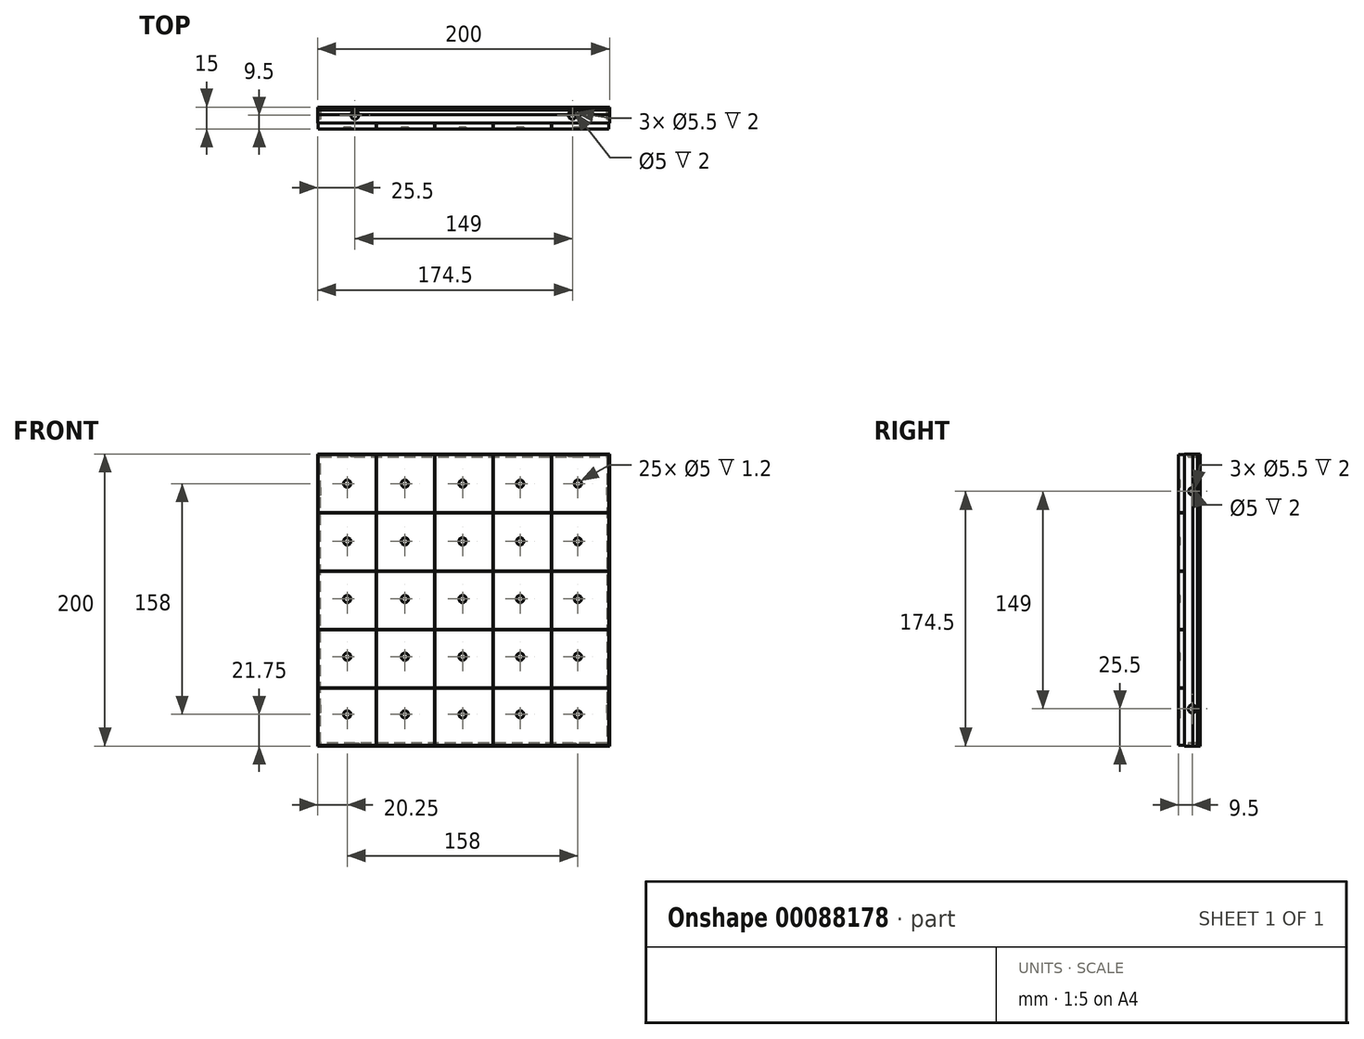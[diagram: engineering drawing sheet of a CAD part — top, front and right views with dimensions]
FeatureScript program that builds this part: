
annotation { "Feature Type Name" : "Feature", "Feature Type Description" : "" }
export const myFeature = defineFeature(function(context is Context, id is Id, definition is map)
    precondition{}
    {
        {
            var Q0;
            Q0=qCreatedBy(makeId("Front.planeOp"),FACE);
            var sketch = newSketch(context, id + "F0", { "sketchPlane" : qUnion([Q0])});
            skLineSegment(sketch, "E0.bottom", {"start": v(100, -100) * mm, "end": v(-100, -100) * mm});
            skLineSegment(sketch, "E0.top", {"start": v(100, 100) * mm, "end": v(-100, 100) * mm});
            skLineSegment(sketch, "E0.left", {"start": v(100, -100) * mm, "end": v(100, 100) * mm});
            skLineSegment(sketch, "E0.right", {"start": v(-100, -100) * mm, "end": v(-100, 100) * mm});
            skPoint(sketch, "E0.middle", {"position": v(0, 0) * mm});
            skSolve(sketch);
        }
        {
            var Q0;
            Q0=makeQuery(id+"F0.imprint","IMPRINT",FACE,{"disambiguationData":[TD([[makeQuery(id+"F0.imprint","IMPRINT",EDGE,{"derivedFrom":sQuery(id+"F0.wireOp",EDGE,"E0.bottom")}),-1.0]])]});
            var Q1;
            Q1 = qSketchRegion(id + "F0", true);
            extrude(context, id + "F1", {"entities" : qUnion([Q0, Q1]), "depth" : 15 * mm});
        }
        {
            var Q0;
            Q0=makeQuery(id+"F1.opExtrude","CAP_FACE",FACE,{"disambiguationData":[OSD([sQuery(id+"F0.wireOp",EDGE,"E0.bottom"),sQuery(id+"F0.wireOp",EDGE,"E0.top"),sQuery(id+"F0.wireOp",EDGE,"E0.left"),sQuery(id+"F0.wireOp",EDGE,"E0.right")])],"isStart":false});
            var sketch = newSketch(context, id + "F2", { "sketchPlane" : qUnion([Q0])});
            skLineSegment(sketch, "E1.bottom", {"start": v(-100, 100) * mm, "end": v(100, 100) * mm});
            skLineSegment(sketch, "E1.top", {"start": v(-100, 99.5) * mm, "end": v(100, 99.5) * mm});
            skLineSegment(sketch, "E1.left", {"start": v(-100, 100) * mm, "end": v(-100, 99.5) * mm});
            skLineSegment(sketch, "E1.right", {"start": v(100, 100) * mm, "end": v(100, 99.5) * mm});
            skLineSegment(sketch, "E2.0.1.0", {"start": v(-100, 59.5) * mm, "end": v(100, 59.5) * mm});
            skLineSegment(sketch, "E2.0.1.1", {"start": v(-100, 60) * mm, "end": v(100, 60) * mm});
            skLineSegment(sketch, "E2.0.1.2", {"start": v(100, 60) * mm, "end": v(100, 59.5) * mm});
            skLineSegment(sketch, "E2.0.1.3", {"start": v(-100, 60) * mm, "end": v(-100, 59.5) * mm});
            skLineSegment(sketch, "E2.0.2.0", {"start": v(-100, 19.5) * mm, "end": v(100, 19.5) * mm});
            skLineSegment(sketch, "E2.0.2.1", {"start": v(-100, 20) * mm, "end": v(100, 20) * mm});
            skLineSegment(sketch, "E2.0.2.2", {"start": v(100, 20) * mm, "end": v(100, 19.5) * mm});
            skLineSegment(sketch, "E2.0.2.3", {"start": v(-100, 20) * mm, "end": v(-100, 19.5) * mm});
            skLineSegment(sketch, "E2.0.3.0", {"start": v(-100, -20.5) * mm, "end": v(100, -20.5) * mm});
            skLineSegment(sketch, "E2.0.3.1", {"start": v(-100, -20) * mm, "end": v(100, -20) * mm});
            skLineSegment(sketch, "E2.0.3.2", {"start": v(100, -20) * mm, "end": v(100, -20.5) * mm});
            skLineSegment(sketch, "E2.0.3.3", {"start": v(-100, -20) * mm, "end": v(-100, -20.5) * mm});
            skLineSegment(sketch, "E2.0.4.0", {"start": v(-100, -60.5) * mm, "end": v(100, -60.5) * mm});
            skLineSegment(sketch, "E2.0.4.1", {"start": v(-100, -60) * mm, "end": v(100, -60) * mm});
            skLineSegment(sketch, "E2.0.4.2", {"start": v(100, -60) * mm, "end": v(100, -60.5) * mm});
            skLineSegment(sketch, "E2.0.4.3", {"start": v(-100, -60) * mm, "end": v(-100, -60.5) * mm});
            skLineSegment(sketch, "E2.direction1", {"start": v(-100, 99.5) * mm, "end": v(-99.9, 99.5) * mm, "construction": true});
            skLineSegment(sketch, "E2.direction2", {"start": v(-100, 99.5) * mm, "end": v(-100, 59.5) * mm, "construction": true});
            skLineSegment(sketch, "E3.0.0.5", {"start": v(-100, -100.5) * mm, "end": v(100, -100.5) * mm});
            skLineSegment(sketch, "E3.3.0.5", {"start": v(-100, -100) * mm, "end": v(100, -100) * mm});
            skLineSegment(sketch, "E3.6.0.5", {"start": v(100, -100) * mm, "end": v(100, -100.5) * mm});
            skLineSegment(sketch, "E3.9.0.5", {"start": v(-100, -100) * mm, "end": v(-100, -100.5) * mm});
            skSolve(sketch);
        }
        {
            var Q0;
            Q0 = qSketchRegion(id + "F0", true);
            extrude(context, id + "F3", {"entities" : qUnion([Q0]), "depth" : 5 * mm});
        }
        {
            var Q0;
            Q0 = qSketchRegion(id + "F2", true);
            extrude(context, id + "F4", {"entities" : qUnion([Q0]), "operationType" : NewBodyOperationType.REMOVE, "oppositeDirection" : true, "depth" : 4 * mm});
        }
        {
            var Q0;
            {var subQ0=sQuery(id+"F0.wireOp",EDGE,"E0.left");var subQ1=sQuery(id+"F0.wireOp",EDGE,"E0.right");Q0=makeQuery(id+"F4.boolean.opBoolean","SPLIT",FACE,{"disambiguationData":[TD([makeQuery(id+"F4.opExtrude","SWEPT_FACE",FACE,{"disambiguationData":[OSD([sQuery(id+"F2.wireOp",EDGE,"E1.top"),sQuery(id+"F2.wireOp",EDGE,"E2.1.0.0"),sQuery(id+"F2.wireOp",EDGE,"E2.2.0.0")])]})])],"derivedFrom":makeQuery(id+"F1.opExtrude","CAP_FACE",FACE,{"disambiguationData":[OSD([sQuery(id+"F0.wireOp",EDGE,"E0.bottom"),sQuery(id+"F0.wireOp",EDGE,"E0.top"),subQ0,subQ1])],"isStart":false})});}
            var sketch = newSketch(context, id + "F5", { "sketchPlane" : qUnion([Q0])});
            skLineSegment(sketch, "E4.bottom", {"start": v(-100, 100) * mm, "end": v(-99.5, 100) * mm});
            skLineSegment(sketch, "E4.top", {"start": v(-100, -100) * mm, "end": v(-99.5, -100) * mm});
            skLineSegment(sketch, "E4.left", {"start": v(-100, 100) * mm, "end": v(-100, -100) * mm});
            skLineSegment(sketch, "E4.right", {"start": v(-99.5, 100) * mm, "end": v(-99.5, -100) * mm});
            skLineSegment(sketch, "E5.1.0.0", {"start": v(-59.5, 100) * mm, "end": v(-59.5, -100) * mm});
            skLineSegment(sketch, "E5.1.0.1", {"start": v(-60, 100) * mm, "end": v(-60, -100) * mm});
            skLineSegment(sketch, "E5.1.0.2", {"start": v(-60, -100) * mm, "end": v(-59.5, -100) * mm});
            skLineSegment(sketch, "E5.1.0.3", {"start": v(-60, 100) * mm, "end": v(-59.5, 100) * mm});
            skLineSegment(sketch, "E5.2.0.0", {"start": v(-19.5, 100) * mm, "end": v(-19.5, -100) * mm});
            skLineSegment(sketch, "E5.2.0.1", {"start": v(-20, 100) * mm, "end": v(-20, -100) * mm});
            skLineSegment(sketch, "E5.2.0.2", {"start": v(-20, -100) * mm, "end": v(-19.5, -100) * mm});
            skLineSegment(sketch, "E5.2.0.3", {"start": v(-20, 100) * mm, "end": v(-19.5, 100) * mm});
            skLineSegment(sketch, "E5.3.0.0", {"start": v(20.5, 100) * mm, "end": v(20.5, -100) * mm});
            skLineSegment(sketch, "E5.3.0.1", {"start": v(20, 100) * mm, "end": v(20, -100) * mm});
            skLineSegment(sketch, "E5.3.0.2", {"start": v(20, -100) * mm, "end": v(20.5, -100) * mm});
            skLineSegment(sketch, "E5.3.0.3", {"start": v(20, 100) * mm, "end": v(20.5, 100) * mm});
            skLineSegment(sketch, "E5.4.0.0", {"start": v(60.5, 100) * mm, "end": v(60.5, -100) * mm});
            skLineSegment(sketch, "E5.4.0.1", {"start": v(60, 100) * mm, "end": v(60, -100) * mm});
            skLineSegment(sketch, "E5.4.0.2", {"start": v(60, -100) * mm, "end": v(60.5, -100) * mm});
            skLineSegment(sketch, "E5.4.0.3", {"start": v(60, 100) * mm, "end": v(60.5, 100) * mm});
            skLineSegment(sketch, "E5.5.0.0", {"start": v(100.5, 100) * mm, "end": v(100.5, -100) * mm});
            skLineSegment(sketch, "E5.5.0.1", {"start": v(100, 100) * mm, "end": v(100, -100) * mm});
            skLineSegment(sketch, "E5.5.0.2", {"start": v(100, -100) * mm, "end": v(100.5, -100) * mm});
            skLineSegment(sketch, "E5.5.0.3", {"start": v(100, 100) * mm, "end": v(100.5, 100) * mm});
            skLineSegment(sketch, "E5.direction1", {"start": v(-99.5, -100) * mm, "end": v(-59.5, -100) * mm, "construction": true});
            skSolve(sketch);
        }
        {
            var Q0;
            Q0 = qSketchRegion(id + "F5", true);
            extrude(context, id + "F6", {"entities" : qUnion([Q0]), "operationType" : NewBodyOperationType.REMOVE, "oppositeDirection" : true, "depth" : 4 * mm});
        }
        {
            var Q0;
            {var subQ0=sQuery(id+"F0.wireOp",EDGE,"E0.bottom");var subQ1=makeQuery(id+"F1.opExtrude","SWEPT_FACE",FACE,{"disambiguationData":[OSD([subQ0])]});var subQ2=sQuery(id+"F0.wireOp",EDGE,"E0.left");var subQ3=makeQuery(id+"F1.opExtrude","SWEPT_FACE",FACE,{"disambiguationData":[OSD([subQ2])]});var subQ5=sQuery(id+"F0.wireOp",EDGE,"E0.right");Q0=makeQuery(id+"F6.boolean.opBoolean","SPLIT",FACE,{"disambiguationData":[TD([subQ3])],"derivedFrom":makeQuery(id+"F4.boolean.opBoolean","SPLIT",FACE,{"disambiguationData":[TD([subQ1])],"derivedFrom":makeQuery(id+"F1.opExtrude","CAP_FACE",FACE,{"disambiguationData":[OSD([subQ0,sQuery(id+"F0.wireOp",EDGE,"E0.top"),subQ2,subQ5])],"isStart":false})})});}
            var sketch = newSketch(context, id + "F7", { "sketchPlane" : qUnion([Q0])});
            skLineSegment(sketch, "E6.bottom", {"start": v(-100, -100) * mm, "end": v(100, -100) * mm});
            skLineSegment(sketch, "E6.top", {"start": v(-100, -99.5) * mm, "end": v(99.5, -99.5) * mm});
            skLineSegment(sketch, "E6.left", {"start": v(-100, -100) * mm, "end": v(-100, -99.5) * mm});
            skLineSegment(sketch, "E6.right", {"start": v(100, -100) * mm, "end": v(100, -99.5) * mm});
            skLineSegment(sketch, "E7.bottom", {"start": v(100, -100) * mm, "end": v(99.5, -100) * mm});
            skLineSegment(sketch, "E7.top", {"start": v(100, 99.5) * mm, "end": v(99.5, 99.5) * mm});
            skLineSegment(sketch, "E7.left", {"start": v(100, -100) * mm, "end": v(100, 99.5) * mm});
            skLineSegment(sketch, "E7.right", {"start": v(99.5, -99.5) * mm, "end": v(99.5, 99.5) * mm});
            skSolve(sketch);
        }
        {
            var Q0;
            Q0 = qSketchRegion(id + "F7", true);
            extrude(context, id + "F8", {"entities" : qUnion([Q0]), "operationType" : NewBodyOperationType.REMOVE, "oppositeDirection" : true, "depth" : 4 * mm});
        }
        {
            var Q0;
            {var subQ0=makeQuery(id+"F4.opExtrude","SWEPT_FACE",FACE,{"disambiguationData":[OSD([sQuery(id+"F2.wireOp",EDGE,"E1.top")])]});var subQ2=sQuery(id+"F0.wireOp",EDGE,"E0.left");var subQ3=sQuery(id+"F0.wireOp",EDGE,"E0.right");Q0=makeQuery(id+"F6.boolean.opBoolean","SPLIT",FACE,{"disambiguationData":[TD([makeQuery(id+"F6.opExtrude","SWEPT_FACE",FACE,{"disambiguationData":[OSD([sQuery(id+"F5.wireOp",EDGE,"E4.right")])]})])],"derivedFrom":makeQuery(id+"F4.boolean.opBoolean","SPLIT",FACE,{"disambiguationData":[TD([subQ0])],"derivedFrom":makeQuery(id+"F1.opExtrude","CAP_FACE",FACE,{"disambiguationData":[OSD([sQuery(id+"F0.wireOp",EDGE,"E0.bottom"),sQuery(id+"F0.wireOp",EDGE,"E0.top"),subQ2,subQ3])],"isStart":false})})});}
            var sketch = newSketch(context, id + "F9", { "sketchPlane" : qUnion([Q0])});
            skPoint(sketch, "E8", {"position": v(-79.75, 79.75) * mm});
            skPoint(sketch, "E8.positionSnap0", {"position": v(-99.5, 79.75) * mm});
            skPoint(sketch, "E8.positionSnap1", {"position": v(-79.75, 99.5) * mm});
            skCircle(sketch, "E9", {"center": v(-79.75, 79.75) * mm, "radius": 2.5 * mm});
            skCircle(sketch, "E10.0.1.0", {"center": v(-79.75, 40.25) * mm, "radius": 2.5 * mm});
            skCircle(sketch, "E10.0.2.0", {"center": v(-79.75, 0.75) * mm, "radius": 2.5 * mm});
            skCircle(sketch, "E10.0.3.0", {"center": v(-79.75, -38.75) * mm, "radius": 2.5 * mm});
            skCircle(sketch, "E10.0.4.0", {"center": v(-79.75, -78.25) * mm, "radius": 2.5 * mm});
            skCircle(sketch, "E10.1.0.0", {"center": v(-40.25, 79.75) * mm, "radius": 2.5 * mm});
            skCircle(sketch, "E10.1.1.0", {"center": v(-40.25, 40.25) * mm, "radius": 2.5 * mm});
            skCircle(sketch, "E10.1.2.0", {"center": v(-40.25, 0.75) * mm, "radius": 2.5 * mm});
            skCircle(sketch, "E10.1.3.0", {"center": v(-40.25, -38.75) * mm, "radius": 2.5 * mm});
            skCircle(sketch, "E10.1.4.0", {"center": v(-40.25, -78.25) * mm, "radius": 2.5 * mm});
            skCircle(sketch, "E10.2.0.0", {"center": v(-0.75, 79.75) * mm, "radius": 2.5 * mm});
            skCircle(sketch, "E10.2.1.0", {"center": v(-0.75, 40.25) * mm, "radius": 2.5 * mm});
            skCircle(sketch, "E10.2.2.0", {"center": v(-0.75, 0.75) * mm, "radius": 2.5 * mm});
            skCircle(sketch, "E10.2.3.0", {"center": v(-0.75, -38.75) * mm, "radius": 2.5 * mm});
            skCircle(sketch, "E10.2.4.0", {"center": v(-0.75, -78.25) * mm, "radius": 2.5 * mm});
            skCircle(sketch, "E10.3.0.0", {"center": v(38.75, 79.75) * mm, "radius": 2.5 * mm});
            skCircle(sketch, "E10.3.1.0", {"center": v(38.75, 40.25) * mm, "radius": 2.5 * mm});
            skCircle(sketch, "E10.3.2.0", {"center": v(38.75, 0.75) * mm, "radius": 2.5 * mm});
            skCircle(sketch, "E10.3.3.0", {"center": v(38.75, -38.75) * mm, "radius": 2.5 * mm});
            skCircle(sketch, "E10.3.4.0", {"center": v(38.75, -78.25) * mm, "radius": 2.5 * mm});
            skCircle(sketch, "E10.4.0.0", {"center": v(78.25, 79.75) * mm, "radius": 2.5 * mm});
            skCircle(sketch, "E10.4.1.0", {"center": v(78.25, 40.25) * mm, "radius": 2.5 * mm});
            skCircle(sketch, "E10.4.2.0", {"center": v(78.25, 0.75) * mm, "radius": 2.5 * mm});
            skCircle(sketch, "E10.4.3.0", {"center": v(78.25, -38.75) * mm, "radius": 2.5 * mm});
            skCircle(sketch, "E10.4.4.0", {"center": v(78.25, -78.25) * mm, "radius": 2.5 * mm});
            skLineSegment(sketch, "E10.direction1", {"start": v(-79.75, 79.75) * mm, "end": v(-40.25, 79.75) * mm, "construction": true});
            skLineSegment(sketch, "E10.direction2", {"start": v(-79.75, 79.75) * mm, "end": v(-79.75, 40.25) * mm, "construction": true});
            skSolve(sketch);
        }
        {
            var Q0;
            Q0 = qSketchRegion(id + "F9", true);
            extrude(context, id + "F10", {"entities" : qUnion([Q0]), "operationType" : NewBodyOperationType.REMOVE, "oppositeDirection" : true, "depth" : 1.2 * mm});
        }
        {
            var Q0;
            Q0=makeQuery(id+"F1.opExtrude","SWEPT_FACE",FACE,{"disambiguationData":[OSD([sQuery(id+"F0.wireOp",EDGE,"E0.left")])]});
            var sketch = newSketch(context, id + "F11", { "sketchPlane" : qUnion([Q0])});
            skCircle(sketch, "E11", {"center": v(-5.5, -74.5) * mm, "radius": 2.75 * mm});
            skCircle(sketch, "E12", {"center": v(-5.5, 74.5) * mm, "radius": 2.5 * mm});
            skSolve(sketch);
        }
        {
            var Q0;
            Q0 = qSketchRegion(id + "F11", true);
            extrude(context, id + "F12", {"entities" : qUnion([Q0]), "operationType" : NewBodyOperationType.REMOVE, "oppositeDirection" : true, "depth" : 2 * mm});
        }
        {
            var Q0;
            Q0=makeQuery(id+"F1.opExtrude","SWEPT_FACE",FACE,{"disambiguationData":[OSD([sQuery(id+"F0.wireOp",EDGE,"E0.bottom")])]});
            var sketch = newSketch(context, id + "F13", { "sketchPlane" : qUnion([Q0])});
            skCircle(sketch, "E13", {"center": v(-74.5, 5.5) * mm, "radius": 2.75 * mm});
            skCircle(sketch, "E14", {"center": v(74.5, 5.5) * mm, "radius": 2.5 * mm});
            skSolve(sketch);
        }
        {
            var Q0;
            Q0 = qSketchRegion(id + "F13", true);
            extrude(context, id + "F14", {"entities" : qUnion([Q0]), "operationType" : NewBodyOperationType.REMOVE, "oppositeDirection" : true, "depth" : 2 * mm});
        }
        {
            var Q0;
            Q0=makeQuery(id+"F1.opExtrude","CAP_FACE",FACE,{"disambiguationData":[OSD([sQuery(id+"F0.wireOp",EDGE,"E0.bottom"),sQuery(id+"F0.wireOp",EDGE,"E0.top"),sQuery(id+"F0.wireOp",EDGE,"E0.left"),sQuery(id+"F0.wireOp",EDGE,"E0.right")])],"isStart":true});
            chamfer(context, id + "F15", {"entities" : qUnion([Q0]), "width" : 2 * mm, "tangentPropagation" : true});
        }
        {
            var Q0;
            Q0=makeQuery(id+"F1.opExtrude","SWEPT_FACE",FACE,{"disambiguationData":[OSD([sQuery(id+"F0.wireOp",EDGE,"E0.right")])]});
            var sketch = newSketch(context, id + "F16", { "sketchPlane" : qUnion([Q0])});
            skCircle(sketch, "E15", {"center": v(5.5, -74.5) * mm, "radius": 2.75 * mm});
            skCircle(sketch, "E16", {"center": v(5.5, 74.5) * mm, "radius": 2.75 * mm});
            skSolve(sketch);
        }
        {
            var Q0;
            Q0 = qSketchRegion(id + "F16", true);
            extrude(context, id + "F17", {"entities" : qUnion([Q0]), "operationType" : NewBodyOperationType.REMOVE, "oppositeDirection" : true, "depth" : 2 * mm});
        }
        {
            var Q0;
            Q0=makeQuery(id+"F1.opExtrude","SWEPT_FACE",FACE,{"disambiguationData":[OSD([sQuery(id+"F0.wireOp",EDGE,"E0.top")])]});
            var sketch = newSketch(context, id + "F18", { "sketchPlane" : qUnion([Q0])});
            skCircle(sketch, "E17", {"center": v(74.5, -5.5) * mm, "radius": 2.75 * mm});
            skCircle(sketch, "E18", {"center": v(-74.5, -5.5) * mm, "radius": 2.75 * mm});
            skSolve(sketch);
        }
        {
            var Q0;
            Q0 = qSketchRegion(id + "F18", true);
            extrude(context, id + "F19", {"entities" : qUnion([Q0]), "operationType" : NewBodyOperationType.REMOVE, "oppositeDirection" : true, "depth" : 2 * mm});
        }
        {
            var Q0;
            Q0=makeQuery(id+"F1.opExtrude","SWEPT_BODY",BODY,{"disambiguationData":[OSD([sQuery(id+"F0.wireOp",EDGE,"E0.bottom"),sQuery(id+"F0.wireOp",EDGE,"E0.top"),sQuery(id+"F0.wireOp",EDGE,"E0.left"),sQuery(id+"F0.wireOp",EDGE,"E0.right")])]});
            transform(context, id + "F20", {"entities" : qUnion([Q0]), "transformType" : TransformType.TRANSLATION_3D, "dx" : 0 * mm, "dy" : 0 * mm, "dz" : 0 * mm, "makeCopy" : true});
        }
        {
            var Q0;
            Q0=makeQuery(id+"F20.opPattern","COPY",BODY,{"derivedFrom":makeQuery(id+"F1.opExtrude","SWEPT_BODY",BODY,{"disambiguationData":[OSD([sQuery(id+"F0.wireOp",EDGE,"E0.bottom"),sQuery(id+"F0.wireOp",EDGE,"E0.top"),sQuery(id+"F0.wireOp",EDGE,"E0.left"),sQuery(id+"F0.wireOp",EDGE,"E0.right")])]}),"instanceName":"1"});
            deleteBodies(context, id + "F21", {"entities" : qUnion([Q0])});
        }
    });
